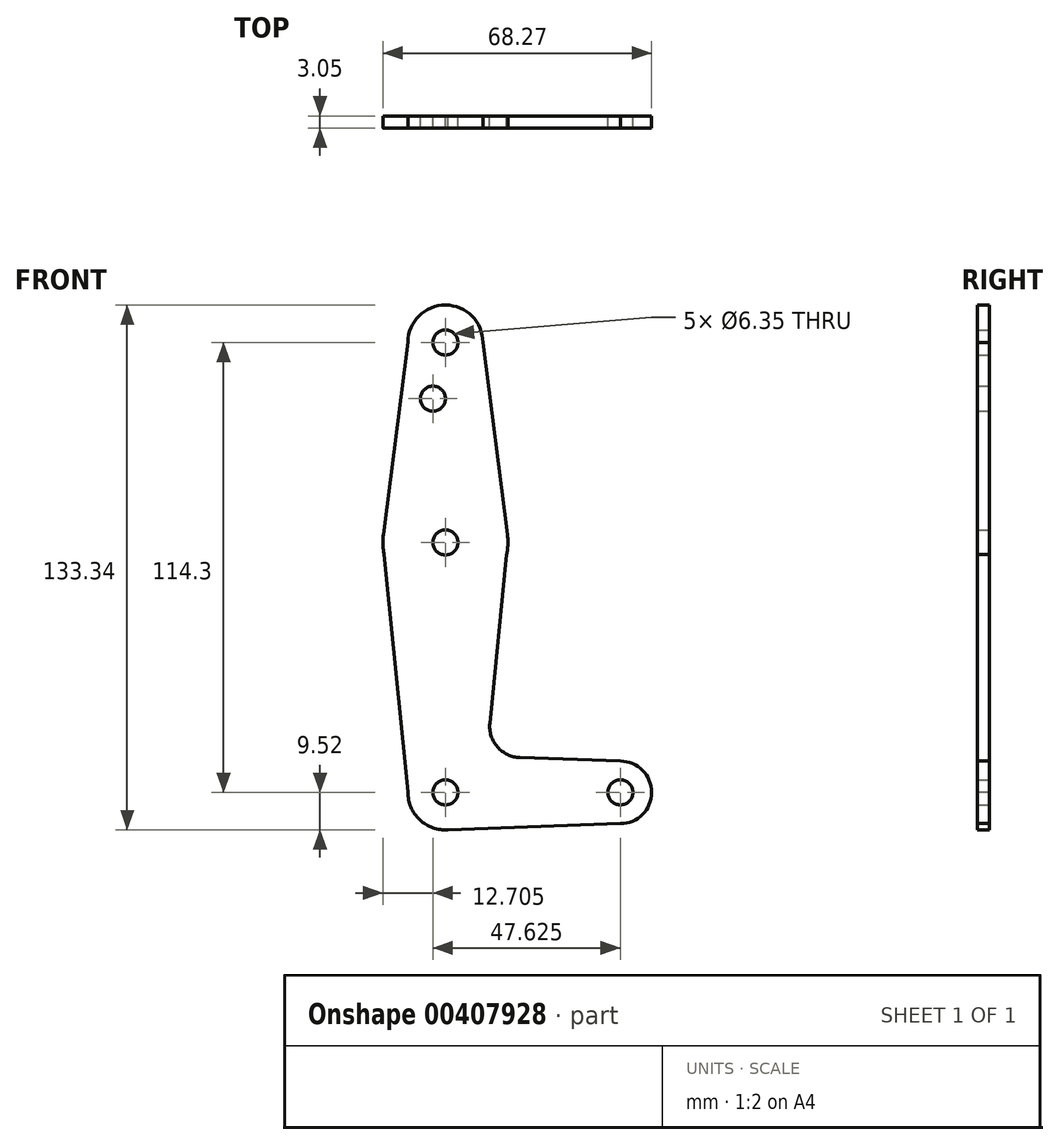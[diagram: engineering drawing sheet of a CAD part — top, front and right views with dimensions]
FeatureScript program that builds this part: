
annotation { "Feature Type Name" : "Feature", "Feature Type Description" : "" }
export const myFeature = defineFeature(function(context is Context, id is Id, definition is map)
    precondition{}
    {
        {
            var Q0;
            Q0=qCreatedBy(makeId("Front.planeOp"),FACE);
            var sketch = newSketch(context, id + "F0", { "sketchPlane" : qUnion([Q0])});
            skLineSegment(sketch, "E0", {"start": v(-44.45, 50.8) * mm, "end": v(-44.45, -63.5) * mm, "construction": true});
            skLineSegment(sketch, "E1", {"start": v(-44.45, -63.5) * mm, "end": v(0, -63.5) * mm, "construction": true});
            skCircle(sketch, "E2", {"center": v(-44.45, 50.8) * mm, "radius": 9.53 * mm});
            skCircle(sketch, "E3", {"center": v(-44.45, 0) * mm, "radius": 15.88 * mm});
            skCircle(sketch, "E4", {"center": v(-44.45, -63.5) * mm, "radius": 9.53 * mm});
            skCircle(sketch, "E5", {"center": v(0, -63.5) * mm, "radius": 7.94 * mm});
            skLineSegment(sketch, "E6", {"start": v(-53.97, 50.87) * mm, "end": v(-60.2, 2) * mm});
            skLineSegment(sketch, "E7", {"start": v(-34.92, 50.8) * mm, "end": v(-28.7, 2) * mm});
            skLineSegment(sketch, "E8", {"start": v(-60.32, -0.08) * mm, "end": v(-53.97, -63.44) * mm});
            skLineSegment(sketch, "E9", {"start": v(-28.58, -0.08) * mm, "end": v(-33.16, -45.91) * mm});
            skLineSegment(sketch, "E10", {"start": v(-25.54, -54.65) * mm, "end": v(0, -55.56) * mm});
            skLineSegment(sketch, "E11", {"start": v(-44.45, -73.02) * mm, "end": v(0, -71.44) * mm});
            skArc(sketch, "E12.filletArc", {"start": v(-33.16, -45.91) * mm, "mid": v(-31.24, -51.93) * mm, "end": v(-25.54, -54.65) * mm});
            skCircle(sketch, "E13", {"center": v(-44.45, 50.8) * mm, "radius": 3.18 * mm});
            skCircle(sketch, "E14", {"center": v(-47.63, 36.53) * mm, "radius": 3.18 * mm});
            skCircle(sketch, "E15", {"center": v(-44.45, 0) * mm, "radius": 3.18 * mm});
            skCircle(sketch, "E16", {"center": v(-44.45, -63.5) * mm, "radius": 3.18 * mm});
            skCircle(sketch, "E17", {"center": v(0, -63.5) * mm, "radius": 3.18 * mm});
            skSolve(sketch);
        }
        {
            var Q0;
            Q0 = qSketchRegion(id + "F0", true);
            extrude(context, id + "F1", {"entities" : qUnion([Q0]), "depth" : 3.05 * mm});
        }
    });
